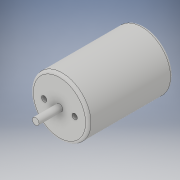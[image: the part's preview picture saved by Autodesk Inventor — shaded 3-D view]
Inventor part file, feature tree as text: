
AUTODESK INVENTOR PART (.ipt)
format: ipt  version: 2018 (Build 220112000, 112)  size: 127,488 bytes
history: native  units: in
note: dims shown in document units (in); Inventor stores cm internally (conversion verified against a paired STEP export)
features: extrude x3, sketch x1, fillet x1
ambient origin geometry x8: Origin, YZ Plane, XZ Plane, XY Plane, X Axis, Y Axis, Z Axis, Center Point
bodies: Solid1 (feature_tree)
feature tree (5):
  sketch  "Sketch1"  dims[d0=2.6772in d1=0.315in d2=0.7087in d3=0.7087in d4=0.25in d5=3.937in d6=0.0in d7=1.0in d8=0.0in d9=1.1024in d10=0.0in d11=0.125in]
  extrude  "Extrusion1"  Depth=0.125in
  extrude  "Extrusion2"  Depth=0.7087in
  extrude  "Extrusion3"  Depth=0.7087in
  fillet  "Fillet1"  Radius=0.25in
